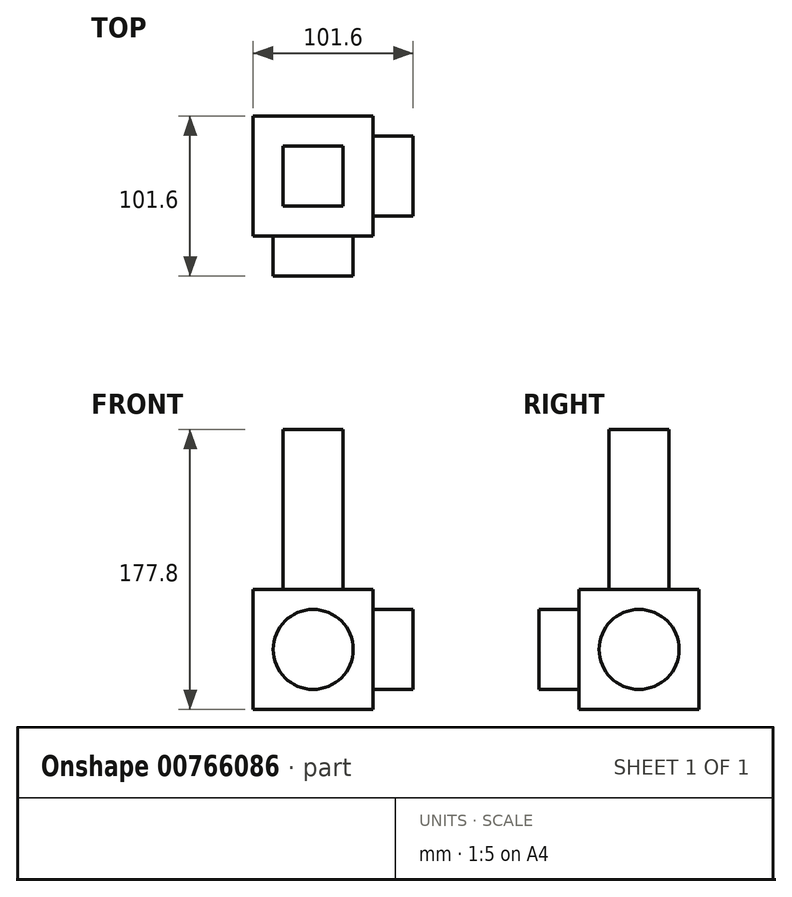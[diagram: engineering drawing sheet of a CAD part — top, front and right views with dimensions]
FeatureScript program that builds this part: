
annotation { "Feature Type Name" : "Feature", "Feature Type Description" : "" }
export const myFeature = defineFeature(function(context is Context, id is Id, definition is map)
    precondition{}
    {
        {
            var Q0;
            Q0=qCreatedBy(makeId("Front.planeOp"),FACE);
            var sketch = newSketch(context, id + "F0", { "sketchPlane" : qUnion([Q0])});
            skLineSegment(sketch, "E0.bottom", {"start": v(-74.9, 72.7) * mm, "end": v(1.3, 72.7) * mm});
            skLineSegment(sketch, "E0.top", {"start": v(-74.9, -3.5) * mm, "end": v(1.3, -3.5) * mm});
            skLineSegment(sketch, "E0.left", {"start": v(-74.9, 72.7) * mm, "end": v(-74.9, -3.5) * mm});
            skLineSegment(sketch, "E0.right", {"start": v(1.3, 72.7) * mm, "end": v(1.3, -3.5) * mm});
            skSolve(sketch);
        }
        {
            var Q0;
            Q0 = qSketchRegion(id + "F0", true);
            extrude(context, id + "F1", {"entities" : qUnion([Q0]), "depth" : 25.4 * mm, "offsetDistance" : 25.4 * mm});
        }
        {
            var Q0;
            Q0=makeQuery(id+"F1.opExtrude","CAP_FACE",FACE,{"disambiguationData":[OSD([sQuery(id+"F0.wireOp",EDGE,"E0.bottom"),sQuery(id+"F0.wireOp",EDGE,"E0.top"),sQuery(id+"F0.wireOp",EDGE,"E0.left"),sQuery(id+"F0.wireOp",EDGE,"E0.right")])],"isStart":false});
            extrude(context, id + "F2", {"entities" : qUnion([Q0]), "operationType" : NewBodyOperationType.ADD, "depth" : 50.8 * mm, "offsetDistance" : 25.4 * mm});
        }
        {
            var Q0;
            Q0=makeQuery(id+"F2.opExtrude","CAP_FACE",FACE,{"disambiguationData":[OSD([sQuery(id+"F0.wireOp",EDGE,"E0.bottom"),sQuery(id+"F0.wireOp",EDGE,"E0.top"),sQuery(id+"F0.wireOp",EDGE,"E0.left"),sQuery(id+"F0.wireOp",EDGE,"E0.right")])],"isStart":false});
            var sketch = newSketch(context, id + "F3", { "sketchPlane" : qUnion([Q0])});
            skPoint(sketch, "E1", {"position": v(-36.8, 34.6) * mm});
            skPoint(sketch, "E1.positionSnap0", {"position": v(1.3, 34.6) * mm});
            skPoint(sketch, "E1.positionSnap1", {"position": v(-36.8, 72.7) * mm});
            skCircle(sketch, "E2", {"center": v(-36.8, 34.6) * mm, "radius": 25.4 * mm});
            skSolve(sketch);
        }
        {
            var Q0;
            Q0 = qSketchRegion(id + "F3", true);
            extrude(context, id + "F4", {"entities" : qUnion([Q0]), "operationType" : NewBodyOperationType.ADD, "depth" : 25.4 * mm, "offsetDistance" : 25.4 * mm});
        }
        {
            var Q0;
            {var subQ0=sQuery(id+"F0.wireOp",EDGE,"E0.right");Q0=makeQuery(id+"F2.boolean.opBoolean","MERGE",FACE,{"derivedFrom":[makeQuery(id+"F1.opExtrude","SWEPT_FACE",FACE,{"disambiguationData":[OSD([subQ0])]}),makeQuery(id+"F2.opExtrude","SWEPT_FACE",FACE,{"disambiguationData":[OSD([subQ0])]})]});}
            var sketch = newSketch(context, id + "F5", { "sketchPlane" : qUnion([Q0])});
            skPoint(sketch, "E3", {"position": v(-38.1, 34.6) * mm});
            skPoint(sketch, "E3.positionSnap0", {"position": v(0, 34.6) * mm});
            skPoint(sketch, "E3.positionSnap1", {"position": v(-38.1, 72.7) * mm});
            skCircle(sketch, "E4", {"center": v(-38.1, 34.6) * mm, "radius": 25.4 * mm});
            skSolve(sketch);
        }
        {
            var Q0;
            Q0 = qSketchRegion(id + "F5", true);
            extrude(context, id + "F6", {"entities" : qUnion([Q0]), "operationType" : NewBodyOperationType.ADD, "depth" : 25.4 * mm, "offsetDistance" : 25.4 * mm});
        }
        {
            var Q0;
            {var subQ0=sQuery(id+"F0.wireOp",EDGE,"E0.bottom");Q0=makeQuery(id+"F2.boolean.opBoolean","MERGE",FACE,{"derivedFrom":[makeQuery(id+"F1.opExtrude","SWEPT_FACE",FACE,{"disambiguationData":[OSD([subQ0])]}),makeQuery(id+"F2.opExtrude","SWEPT_FACE",FACE,{"disambiguationData":[OSD([subQ0])]})]});}
            var sketch = newSketch(context, id + "F7", { "sketchPlane" : qUnion([Q0])});
            skPoint(sketch, "E5", {"position": v(-36.8, -38.1) * mm});
            skPoint(sketch, "E5.positionSnap0", {"position": v(-36.8, 0) * mm});
            skPoint(sketch, "E5.positionSnap1", {"position": v(-74.9, -38.1) * mm});
            skLineSegment(sketch, "E6.bottom", {"start": v(-17.76, -57.15) * mm, "end": v(-55.86, -57.15) * mm});
            skLineSegment(sketch, "E6.top", {"start": v(-17.76, -19.05) * mm, "end": v(-55.86, -19.05) * mm});
            skLineSegment(sketch, "E6.left", {"start": v(-17.76, -57.15) * mm, "end": v(-17.76, -19.05) * mm});
            skLineSegment(sketch, "E6.right", {"start": v(-55.86, -57.15) * mm, "end": v(-55.86, -19.05) * mm});
            skSolve(sketch);
        }
        {
            var Q0;
            Q0 = qSketchRegion(id + "F7", true);
            extrude(context, id + "F8", {"entities" : qUnion([Q0]), "operationType" : NewBodyOperationType.ADD, "depth" : 101.6 * mm, "offsetDistance" : 25.4 * mm});
        }
    });
